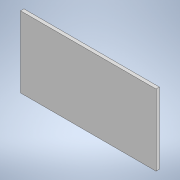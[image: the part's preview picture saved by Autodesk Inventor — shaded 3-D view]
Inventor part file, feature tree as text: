
AUTODESK INVENTOR PART (.ipt)
format: ipt  version: 2022 (Build 260153000, 153)  size: 88,576 bytes
history: native  units: mm
features: sketch x2, extrude x1
ambient origin geometry x8: Origin, YZ Plane, XZ Plane, XY Plane, X Axis, Y Axis, Z Axis, Center Point
bodies: Solid1 (feature_tree)
feature tree (3):
  sketch  "Sketch1"  dims[d0=40.0mm d1=21.0mm]
  extrude  "Extrusion1"  Depth=21.0mm
  sketch  "Sketch2"  dims[d2=1.0mm d3=0.0mm]
